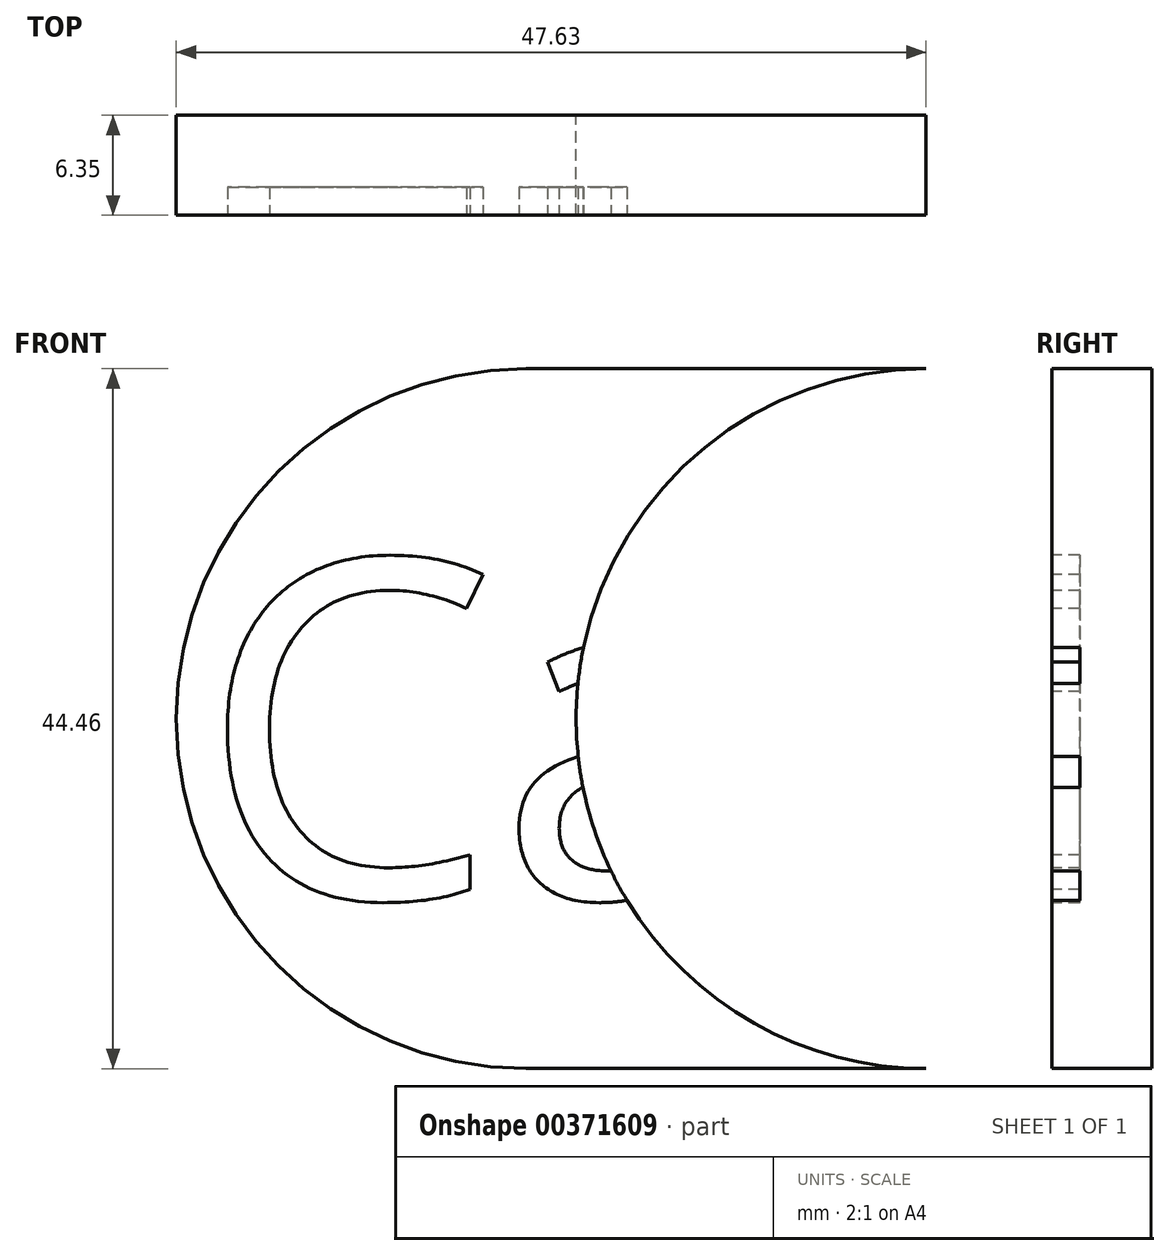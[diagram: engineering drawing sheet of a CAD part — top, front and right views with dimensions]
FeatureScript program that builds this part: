
annotation { "Feature Type Name" : "Feature", "Feature Type Description" : "" }
export const myFeature = defineFeature(function(context is Context, id is Id, definition is map)
    precondition{}
    {
        {
            var Q0;
            Q0=qCreatedBy(makeId("Front.planeOp"),FACE);
            var sketch = newSketch(context, id + "F0", { "sketchPlane" : qUnion([Q0])});
            skCircle(sketch, "E0", {"center": v(0, 0) * mm, "radius": 22.23 * mm});
            skCircle(sketch, "E1", {"center": v(25.4, 0) * mm, "radius": 22.23 * mm});
            skLineSegment(sketch, "E2", {"start": v(0, 22.22) * mm, "end": v(25.4, 22.22) * mm});
            skLineSegment(sketch, "E3", {"start": v(0, -22.23) * mm, "end": v(25.4, -22.23) * mm});
            skSolve(sketch);
        }
        {
            var Q0;
            {var subQ0=sQuery(id+"F0.wireOp",EDGE,"E1");var subQ1=sQuery(id+"F0.wireOp",EDGE,"E0");var subQ2=makeQuery(id+"F0.imprint","INTERSECT",VERTEX,{"disambiguationData":[OD(0.0)],"derivedFrom":[subQ1,subQ0]});Q0=makeQuery(id+"F0.imprint","IMPRINT",FACE,{"disambiguationData":[TD([[makeQuery(id+"F0.imprint","IMPRINT",EDGE,{"disambiguationData":[TD([[subQ2,1.0]])],"derivedFrom":subQ1}),1.0]])]});}
            var Q1;
            {var subQ0=sQuery(id+"F0.wireOp",EDGE,"E2");Q1=makeQuery(id+"F0.imprint","IMPRINT",FACE,{"disambiguationData":[TD([[makeQuery(id+"F0.imprint","IMPRINT",EDGE,{"derivedFrom":subQ0}),-1.0]])]});}
            var Q2;
            {var subQ0=sQuery(id+"F0.wireOp",EDGE,"E3");Q2=makeQuery(id+"F0.imprint","IMPRINT",FACE,{"disambiguationData":[TD([[makeQuery(id+"F0.imprint","IMPRINT",EDGE,{"derivedFrom":subQ0}),1.0]])]});}
            var Q3;
            {var subQ0=sQuery(id+"F0.wireOp",EDGE,"E0");var subQ1=makeQuery(id+"F0.imprint","INTERSECT",VERTEX,{"derivedFrom":[subQ0,sQuery(id+"F0.wireOp",EDGE,"E2")]});Q3=makeQuery(id+"F0.imprint","IMPRINT",FACE,{"disambiguationData":[TD([[makeQuery(id+"F0.imprint","IMPRINT",EDGE,{"disambiguationData":[TD([[subQ1,1.0]])],"derivedFrom":subQ0}),1.0]])]});}
            var Q4;
            {var subQ0=sQuery(id+"F0.wireOp",EDGE,"E1");var subQ1=sQuery(id+"F0.wireOp",EDGE,"E0");var subQ2=makeQuery(id+"F0.imprint","INTERSECT",VERTEX,{"disambiguationData":[OD(0.0)],"derivedFrom":[subQ1,subQ0]});Q4=makeQuery(id+"F0.imprint","IMPRINT",FACE,{"disambiguationData":[TD([[makeQuery(id+"F0.imprint","IMPRINT",EDGE,{"disambiguationData":[TD([[subQ2,1.0]])],"derivedFrom":subQ1}),-1.0]])]});}
            extrude(context, id + "F1", {"entities" : qUnion([Q0, Q1, Q2, Q3, Q4]), "depth" : 6.35 * mm});
        }
        {
            var Q0;
            Q0=makeQuery(id+"F1.opExtrude","CAP_FACE",FACE,{"disambiguationData":[OSD([sQuery(id+"F0.wireOp",EDGE,"E0"),sQuery(id+"F0.wireOp",EDGE,"E1"),sQuery(id+"F0.wireOp",EDGE,"E2"),sQuery(id+"F0.wireOp",EDGE,"E3")])],"isStart":false});
            var sketch = newSketch(context, id + "F2", { "sketchPlane" : qUnion([Q0])});
            skCircle(sketch, "E4", {"center": v(37.1, 0) * mm, "radius": 3.18 * mm});
            skSolve(sketch);
        }
        {
            var Q0;
            Q0 = qSketchRegion(id + "F2", true);
            extrude(context, id + "F3", {"entities" : qUnion([Q0]), "operationType" : NewBodyOperationType.REMOVE, "oppositeDirection" : true, "depth" : 25.4 * mm});
        }
        {
            var Q0;
            Q0=makeQuery(id+"F1.opExtrude","CAP_FACE",FACE,{"disambiguationData":[OSD([sQuery(id+"F0.wireOp",EDGE,"E0"),sQuery(id+"F0.wireOp",EDGE,"E1"),sQuery(id+"F0.wireOp",EDGE,"E2"),sQuery(id+"F0.wireOp",EDGE,"E3")])],"isStart":false});
            var sketch = newSketch(context, id + "F4", { "sketchPlane" : qUnion([Q0])});
            skText(sketch, "E5", { "text": "Carl", "fontName": "OpenSans-Regular.ttf"});
            const initialGuessF4  = {"E5": [-0.02081, -0.01139, 1, 0, 0.02165]};
            skSetInitialGuess(sketch, initialGuessF4);
            skSolve(sketch);
        }
        {
            var Q0;
            Q0 = qSketchRegion(id + "F4", true);
            extrude(context, id + "F5", {"entities" : qUnion([Q0]), "operationType" : NewBodyOperationType.REMOVE, "oppositeDirection" : true, "depth" : 1.78 * mm});
        }
    });
